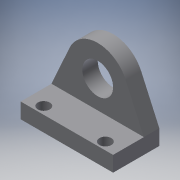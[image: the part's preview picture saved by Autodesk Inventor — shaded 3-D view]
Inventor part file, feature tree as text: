
AUTODESK INVENTOR PART (.ipt)
format: ipt  version: 2018 (Build 220112000, 112)  size: 125,440 bytes
history: native  units: in
note: dims shown in document units (in); Inventor stores cm internally (conversion verified against a paired STEP export)
features: other x3, extrude x2, sketch x2, projected_geometry x1, reference x1
ambient origin geometry x8: Origin, YZ Plane, XZ Plane, XY Plane, X Axis, Y Axis, Z Axis, Center Point
bodies: Solid1 (feature_tree)
feature tree (9):
  extrude  "Extrusion1"  Depth=0.195in
  extrude  "Extrusion2"  Depth=0.25in
  sketch  "Sketch1"  dims[d0=0.195in d1=0.195in]
  sketch  "Sketch2"  dims[d2=1.0in d3=0.25in d4=0.125in d5=0.25in d6=0.75in d7=0.25in d8=0.0in d9=0.25in d10=0.5in d11=0.25in d12=0.0in]
  projected_geometry  "Projected Loop1"
  reference  "Reference1"
  parser-record x1  (decoder bookkeeping rows leaked as tree rows — omitted from the tree; the rows remain in map.json)
  other  "Assembly2.iam"
  other  "0_375_Hex_ID_x_1_125_OD_x_0_313_WD_Flanged_Bearing_217-2735:2"
note: 1 file-system path scrubbed to <path> (originals preserved in map.json)
